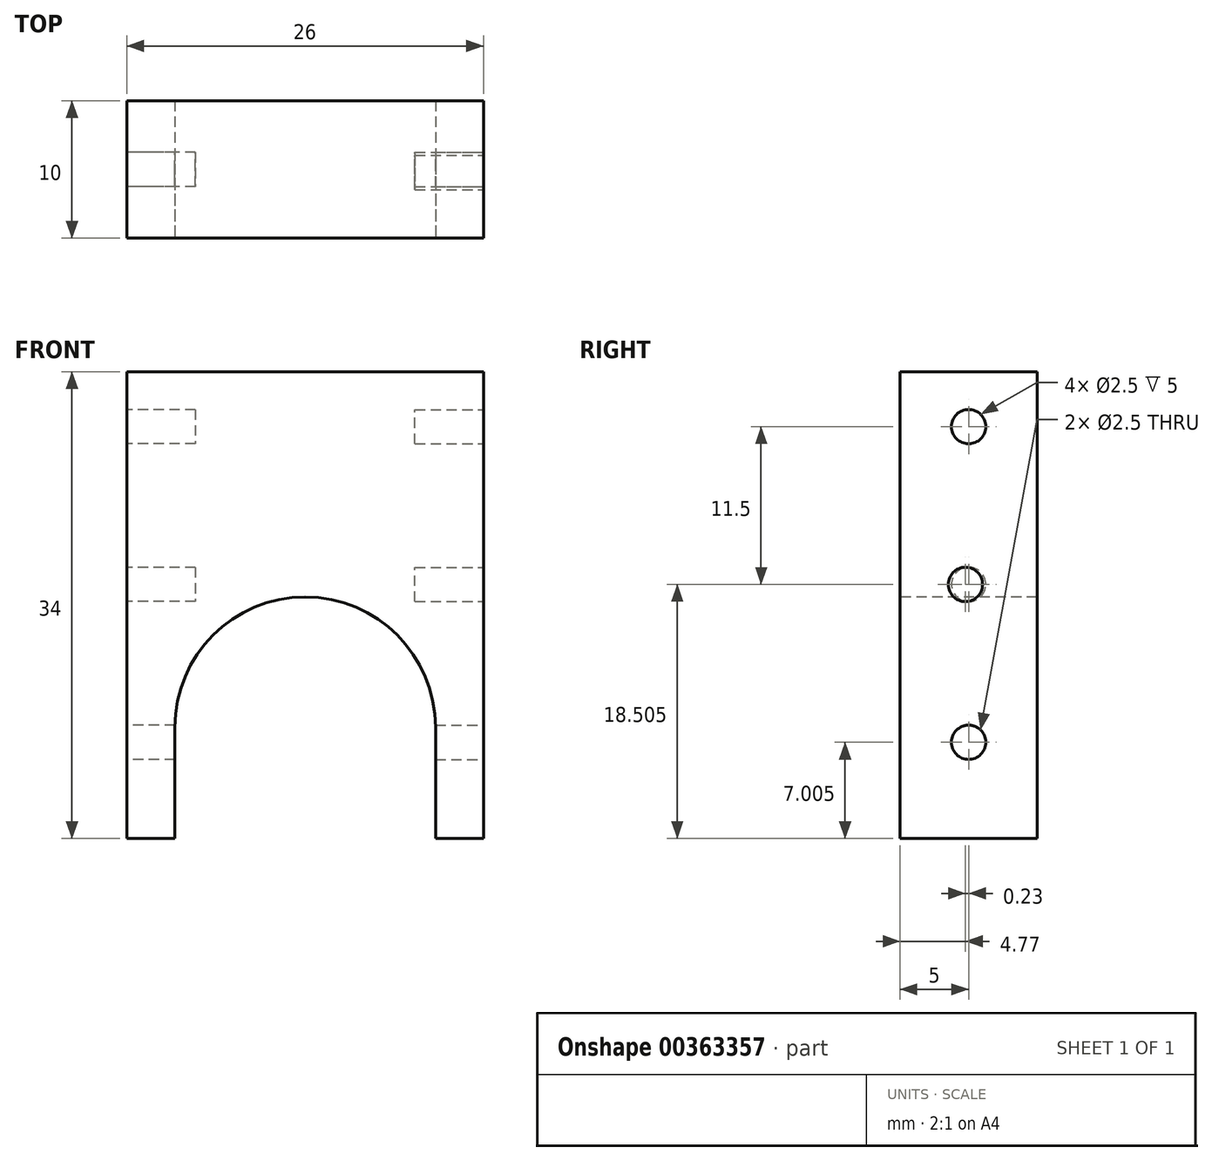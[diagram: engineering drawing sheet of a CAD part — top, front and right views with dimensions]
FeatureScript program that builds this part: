
annotation { "Feature Type Name" : "Feature", "Feature Type Description" : "" }
export const myFeature = defineFeature(function(context is Context, id is Id, definition is map)
    precondition{}
    {
        {
            var Q0;
            Q0=qCreatedBy(makeId("Front.planeOp"),FACE);
            var sketch = newSketch(context, id + "F0", { "sketchPlane" : qUnion([Q0])});
            skLineSegment(sketch, "E0.bottom", {"start": v(-51.61, 15.82) * mm, "end": v(-25.61, 15.82) * mm});
            skLineSegment(sketch, "E0.top", {"start": v(-51.61, -18.18) * mm, "end": v(-48.11, -18.18) * mm});
            skLineSegment(sketch, "E0.left", {"start": v(-51.61, 15.82) * mm, "end": v(-51.61, -18.18) * mm});
            skLineSegment(sketch, "E0.right", {"start": v(-25.61, 15.82) * mm, "end": v(-25.61, -18.18) * mm});
            skLineSegment(sketch, "E1", {"start": v(-48.11, -18.18) * mm, "end": v(-48.11, -10.09) * mm});
            skLineSegment(sketch, "E2", {"start": v(-29.11, -18.18) * mm, "end": v(-29.11, -10.09) * mm});
            skArc(sketch, "E3", {"start": v(-29.11, -10.09) * mm, "mid": v(-38.61, -0.59) * mm, "end": v(-48.11, -10.09) * mm});
            skPoint(sketch, "E3.first.point", {"position": v(-38.61, -0.59) * mm});
            skPoint(sketch, "E3.third.point", {"position": v(-29.11, -10.09) * mm});
            skLineSegment(sketch, "E4.trimOffspring", {"start": v(-29.11, -18.18) * mm, "end": v(-25.61, -18.18) * mm});
            skSolve(sketch);
        }
        {
            var Q0;
            Q0=makeQuery(id+"F0.imprint","IMPRINT",FACE,{"disambiguationData":[TD([[makeQuery(id+"F0.imprint","IMPRINT",EDGE,{"derivedFrom":sQuery(id+"F0.wireOp",EDGE,"E0.bottom")}),-1.0]])]});
            extrude(context, id + "F1", {"entities" : qUnion([Q0]), "oppositeDirection" : true, "depth" : 10 * mm});
        }
        {
            var Q0;
            Q0=makeQuery(id+"F1.opExtrude","SWEPT_FACE",FACE,{"disambiguationData":[OSD([sQuery(id+"F0.wireOp",EDGE,"E0.right")])]});
            var sketch = newSketch(context, id + "F2", { "sketchPlane" : qUnion([Q0])});
            skCircle(sketch, "E5", {"center": v(4.77, 0.32) * mm, "radius": 1.25 * mm});
            skCircle(sketch, "E6", {"center": v(5, 11.82) * mm, "radius": 1.25 * mm});
            skCircle(sketch, "E7", {"center": v(5, -11.18) * mm, "radius": 1.25 * mm});
            skSolve(sketch);
        }
        {
            var Q0;
            Q0=qSketchRegion(id+"F2",true);
            extrude(context, id + "F3", {"entities" : qUnion([Q0]), "operationType" : NewBodyOperationType.REMOVE, "oppositeDirection" : true, "depth" : 5 * mm});
        }
        {
            var Q0;
            Q0=makeQuery(id+"F1.opExtrude","SWEPT_FACE",FACE,{"disambiguationData":[OSD([sQuery(id+"F0.wireOp",EDGE,"E0.left")])]});
            var sketch = newSketch(context, id + "F4", { "sketchPlane" : qUnion([Q0])});
            skCircle(sketch, "E8", {"center": v(-5, 11.82) * mm, "radius": 1.25 * mm});
            skCircle(sketch, "E9", {"center": v(-5, 0.32) * mm, "radius": 1.25 * mm});
            skCircle(sketch, "E10", {"center": v(-5, -11.18) * mm, "radius": 1.25 * mm});
            skSolve(sketch);
        }
        {
            var Q0;
            Q0=qSketchRegion(id+"F4",true);
            extrude(context, id + "F5", {"entities" : qUnion([Q0]), "operationType" : NewBodyOperationType.REMOVE, "oppositeDirection" : true, "depth" : 5 * mm});
        }
    });
